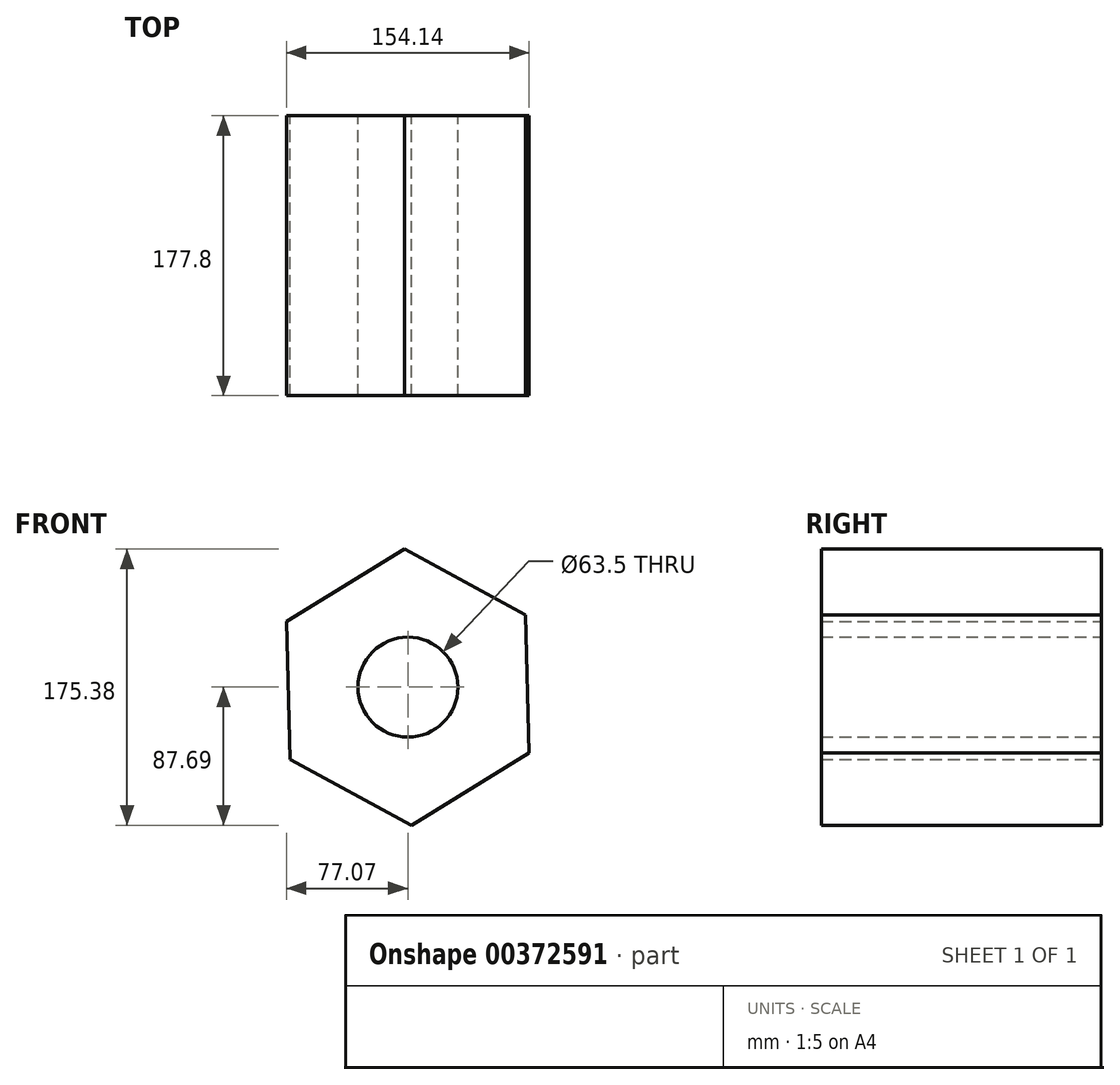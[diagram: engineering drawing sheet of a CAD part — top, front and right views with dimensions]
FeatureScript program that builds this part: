
annotation { "Feature Type Name" : "Feature", "Feature Type Description" : "" }
export const myFeature = defineFeature(function(context is Context, id is Id, definition is map)
    precondition{}
    {
        {
            var Q0;
            Q0=qCreatedBy(makeId("Front.planeOp"),FACE);
            var sketch = newSketch(context, id + "F0", { "sketchPlane" : qUnion([Q0])});
            skCircle(sketch, "E0.cCircle", {"center": v(0, 0) * mm, "radius": 87.72 * mm, "construction": true});
            skLineSegment(sketch, "E0.0", {"start": v(77.07, -41.9) * mm, "end": v(2.25, -87.69) * mm});
            skLineSegment(sketch, "E0.1", {"start": v(2.25, -87.69) * mm, "end": v(-74.81, -45.8) * mm});
            skLineSegment(sketch, "E0.2", {"start": v(-74.81, -45.8) * mm, "end": v(-77.07, 41.9) * mm});
            skLineSegment(sketch, "E0.3", {"start": v(-77.07, 41.9) * mm, "end": v(-2.25, 87.69) * mm});
            skLineSegment(sketch, "E0.4", {"start": v(-2.25, 87.69) * mm, "end": v(74.81, 45.8) * mm});
            skLineSegment(sketch, "E0.5", {"start": v(74.81, 45.8) * mm, "end": v(77.07, -41.9) * mm});
            skSolve(sketch);
        }
        {
            var Q0;
            Q0=makeQuery(id+"F0.imprint","IMPRINT",FACE,{"disambiguationData":[TD([[makeQuery(id+"F0.imprint","IMPRINT",EDGE,{"derivedFrom":sQuery(id+"F0.wireOp",EDGE,"E0.0")}),-1.0]])]});
            extrude(context, id + "F1", {"entities" : qUnion([Q0]), "depth" : 177.8 * mm});
        }
        {
            var Q0;
            Q0=sQuery(id+"F0.wireOp",VERTEX,"E0.cCircle.center");
            var Q1;
            Q1=makeQuery(id+"F1.opExtrude","SWEPT_BODY",BODY,{"disambiguationData":[OSD([sQuery(id+"F0.wireOp",EDGE,"E0.0"),sQuery(id+"F0.wireOp",EDGE,"E0.1"),sQuery(id+"F0.wireOp",EDGE,"E0.2"),sQuery(id+"F0.wireOp",EDGE,"E0.3"),sQuery(id+"F0.wireOp",EDGE,"E0.4"),sQuery(id+"F0.wireOp",EDGE,"E0.5")])]});
            hole(context, id + "F2", {"style" : HoleStyle.SIMPLE, "endStyle" : HoleEndStyle.THROUGH, "oppositeDirection" : true, "holeDiameter" : 63.5 * mm, "isTappedThrough" : true, "tappedDepth" : 12.7 * mm, "tapClearance" : 3, "locations" : qUnion([Q0]), "scope" : qUnion([Q1])});
        }
    });
